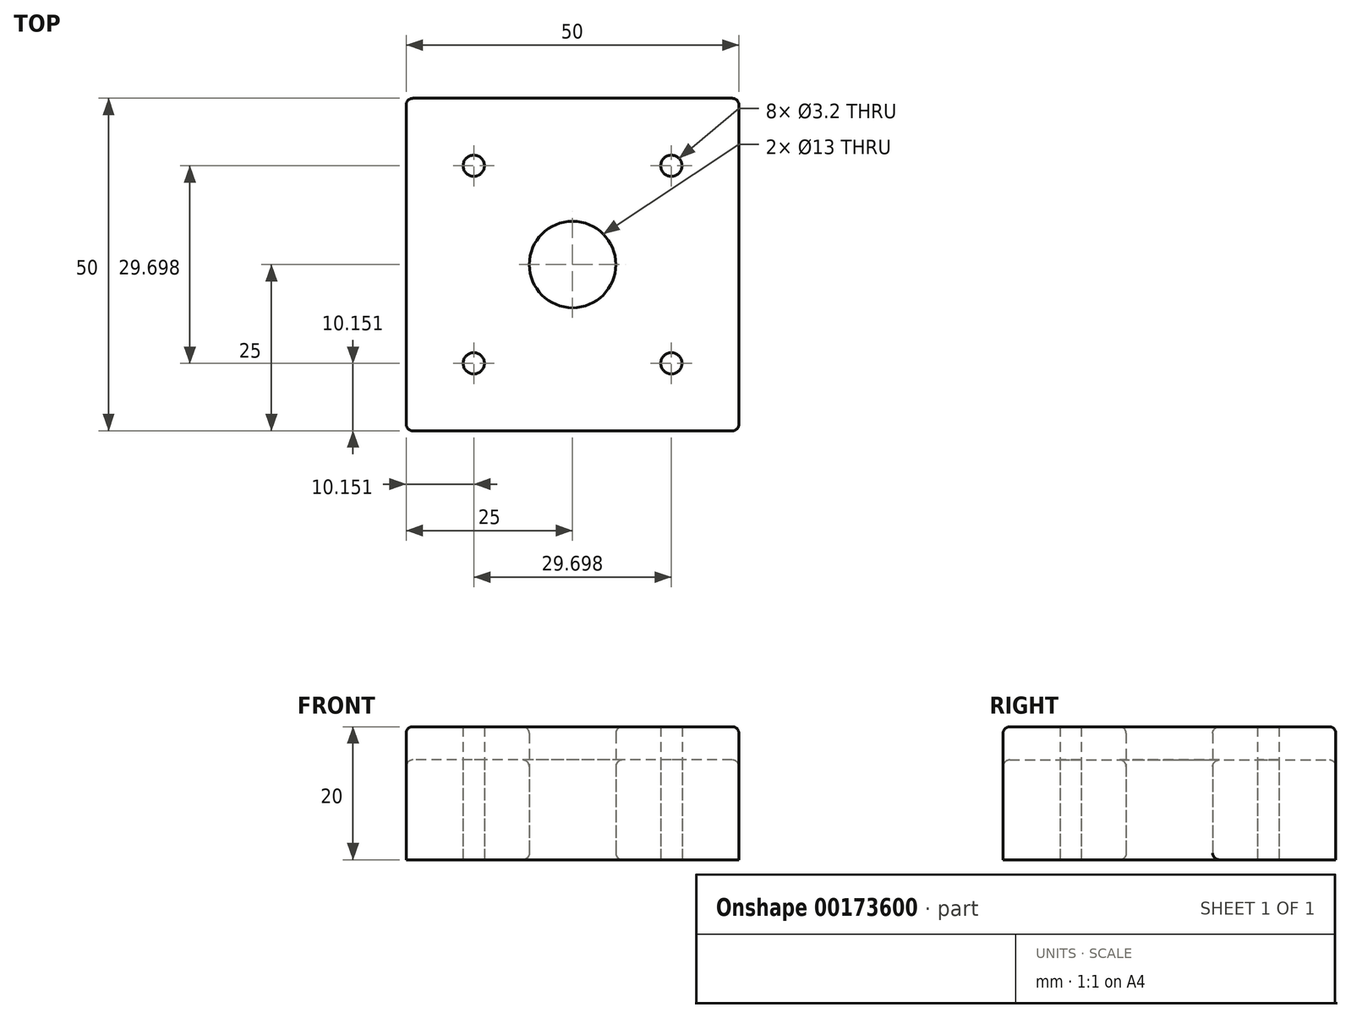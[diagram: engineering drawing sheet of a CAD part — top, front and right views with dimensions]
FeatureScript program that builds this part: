
annotation { "Feature Type Name" : "Feature", "Feature Type Description" : "" }
export const myFeature = defineFeature(function(context is Context, id is Id, definition is map)
    precondition{}
    {
        {
            var Q0;
            Q0=qCreatedBy(makeId("Top.planeOp"),FACE);
            var sketch = newSketch(context, id + "F0", { "sketchPlane" : qUnion([Q0])});
            skLineSegment(sketch, "E0.bottom", {"start": v(25, -25) * mm, "end": v(-25, -25) * mm});
            skLineSegment(sketch, "E0.top", {"start": v(25, 25) * mm, "end": v(-25, 25) * mm});
            skLineSegment(sketch, "E0.left", {"start": v(25, -25) * mm, "end": v(25, 25) * mm});
            skLineSegment(sketch, "E0.right", {"start": v(-25, -25) * mm, "end": v(-25, 25) * mm});
            skPoint(sketch, "E0.middle", {"position": v(0, 0) * mm});
            skCircle(sketch, "E1", {"center": v(0, 0) * mm, "radius": 6.5 * mm});
            skLineSegment(sketch, "E2", {"start": v(-25, 25) * mm, "end": v(25, -25) * mm, "construction": true});
            skLineSegment(sketch, "E3", {"start": v(25, 25) * mm, "end": v(-25, -25) * mm, "construction": true});
            skCircle(sketch, "E4", {"center": v(-14.85, -14.85) * mm, "radius": 1.6 * mm});
            skCircle(sketch, "E5", {"center": v(-14.85, 14.85) * mm, "radius": 1.6 * mm});
            skCircle(sketch, "E6", {"center": v(14.85, 14.85) * mm, "radius": 1.6 * mm});
            skCircle(sketch, "E7", {"center": v(14.85, -14.85) * mm, "radius": 1.6 * mm});
            skSolve(sketch);
        }
        {
            var Q0;
            Q0 = qSketchRegion(id + "F0", true);
            extrude(context, id + "F1", {"entities" : qUnion([Q0]), "depth" : 15 * mm});
        }
        {
            var Q0;
            Q0=makeQuery(id+"F1.opExtrude","SWEPT_EDGE",EDGE,{"disambiguationData":[OSD([sQuery(id+"F0.wireOp",EDGE,"E0.bottom"),sQuery(id+"F0.wireOp",EDGE,"E0.right")])]});
            var Q1;
            Q1=makeQuery(id+"F1.opExtrude","SWEPT_EDGE",EDGE,{"disambiguationData":[OSD([sQuery(id+"F0.wireOp",EDGE,"E0.bottom"),sQuery(id+"F0.wireOp",EDGE,"E0.left")])]});
            var Q2;
            Q2=makeQuery(id+"F1.opExtrude","SWEPT_EDGE",EDGE,{"disambiguationData":[OSD([sQuery(id+"F0.wireOp",EDGE,"E0.top"),sQuery(id+"F0.wireOp",EDGE,"E0.left")])]});
            var Q3;
            Q3=makeQuery(id+"F1.opExtrude","SWEPT_EDGE",EDGE,{"disambiguationData":[OSD([sQuery(id+"F0.wireOp",EDGE,"E0.top"),sQuery(id+"F0.wireOp",EDGE,"E0.right")])]});
            var Q4;
            Q4=makeQuery(id+"F1.opExtrude","CAP_EDGE",EDGE,{"disambiguationData":[OSD([sQuery(id+"F0.wireOp",EDGE,"E0.top")])],"isStart":false});
            var Q5;
            Q5=makeQuery(id+"F1.opExtrude","CAP_EDGE",EDGE,{"disambiguationData":[OSD([sQuery(id+"F0.wireOp",EDGE,"E0.left")])],"isStart":false});
            var Q6;
            Q6=makeQuery(id+"F1.opExtrude","CAP_EDGE",EDGE,{"disambiguationData":[OSD([sQuery(id+"F0.wireOp",EDGE,"E0.bottom")])],"isStart":false});
            var Q7;
            Q7=makeQuery(id+"F1.opExtrude","CAP_EDGE",EDGE,{"disambiguationData":[OSD([sQuery(id+"F0.wireOp",EDGE,"E0.right")])],"isStart":false});
            var Q8;
            Q8=makeQuery(id+"F1.opExtrude","CAP_EDGE",EDGE,{"disambiguationData":[OSD([sQuery(id+"F0.wireOp",EDGE,"E1")])],"isStart":false});
            var Q9;
            Q9=makeQuery(id+"F1.opExtrude","CAP_EDGE",EDGE,{"disambiguationData":[OSD([sQuery(id+"F0.wireOp",EDGE,"E1")])],"isStart":true});
            fillet(context, id + "F2", {"entities" : qUnion([Q0, Q1, Q2, Q3, Q4, Q5, Q6, Q7, Q8, Q9]), "radius" : 1 * mm, "tangentPropagation" : true, "allowEdgeOverflow" : false});
        }
        {
            var Q0;
            Q0 = qSketchRegion(id + "F0", true);
            extrude(context, id + "F3", {"entities" : qUnion([Q0]), "depth" : 20 * mm});
        }
        {
            var Q0;
            Q0=makeQuery(id+"F3.opExtrude","SWEPT_EDGE",EDGE,{"disambiguationData":[OSD([sQuery(id+"F0.wireOp",EDGE,"E0.bottom"),sQuery(id+"F0.wireOp",EDGE,"E0.right")])]});
            var Q1;
            Q1=makeQuery(id+"F3.opExtrude","SWEPT_EDGE",EDGE,{"disambiguationData":[OSD([sQuery(id+"F0.wireOp",EDGE,"E0.bottom"),sQuery(id+"F0.wireOp",EDGE,"E0.left")])]});
            var Q2;
            Q2=makeQuery(id+"F3.opExtrude","SWEPT_EDGE",EDGE,{"disambiguationData":[OSD([sQuery(id+"F0.wireOp",EDGE,"E0.top"),sQuery(id+"F0.wireOp",EDGE,"E0.left")])]});
            var Q3;
            Q3=makeQuery(id+"F3.opExtrude","SWEPT_EDGE",EDGE,{"disambiguationData":[OSD([sQuery(id+"F0.wireOp",EDGE,"E0.top"),sQuery(id+"F0.wireOp",EDGE,"E0.right")])]});
            var Q4;
            Q4=makeQuery(id+"F3.opExtrude","CAP_EDGE",EDGE,{"disambiguationData":[OSD([sQuery(id+"F0.wireOp",EDGE,"E0.top")])],"isStart":false});
            var Q5;
            Q5=makeQuery(id+"F3.opExtrude","CAP_EDGE",EDGE,{"disambiguationData":[OSD([sQuery(id+"F0.wireOp",EDGE,"E0.right")])],"isStart":false});
            var Q6;
            Q6=makeQuery(id+"F3.opExtrude","CAP_EDGE",EDGE,{"disambiguationData":[OSD([sQuery(id+"F0.wireOp",EDGE,"E0.bottom")])],"isStart":false});
            var Q7;
            Q7=makeQuery(id+"F3.opExtrude","CAP_EDGE",EDGE,{"disambiguationData":[OSD([sQuery(id+"F0.wireOp",EDGE,"E0.left")])],"isStart":false});
            var Q8;
            Q8=makeQuery(id+"F3.opExtrude","CAP_EDGE",EDGE,{"disambiguationData":[OSD([sQuery(id+"F0.wireOp",EDGE,"E1")])],"isStart":false});
            var Q9;
            Q9=makeQuery(id+"F3.opExtrude","CAP_EDGE",EDGE,{"disambiguationData":[OSD([sQuery(id+"F0.wireOp",EDGE,"E1")])],"isStart":true});
            fillet(context, id + "F4", {"entities" : qUnion([Q0, Q1, Q2, Q3, Q4, Q5, Q6, Q7, Q8, Q9]), "radius" : 1 * mm, "tangentPropagation" : true, "allowEdgeOverflow" : false});
        }
    });
